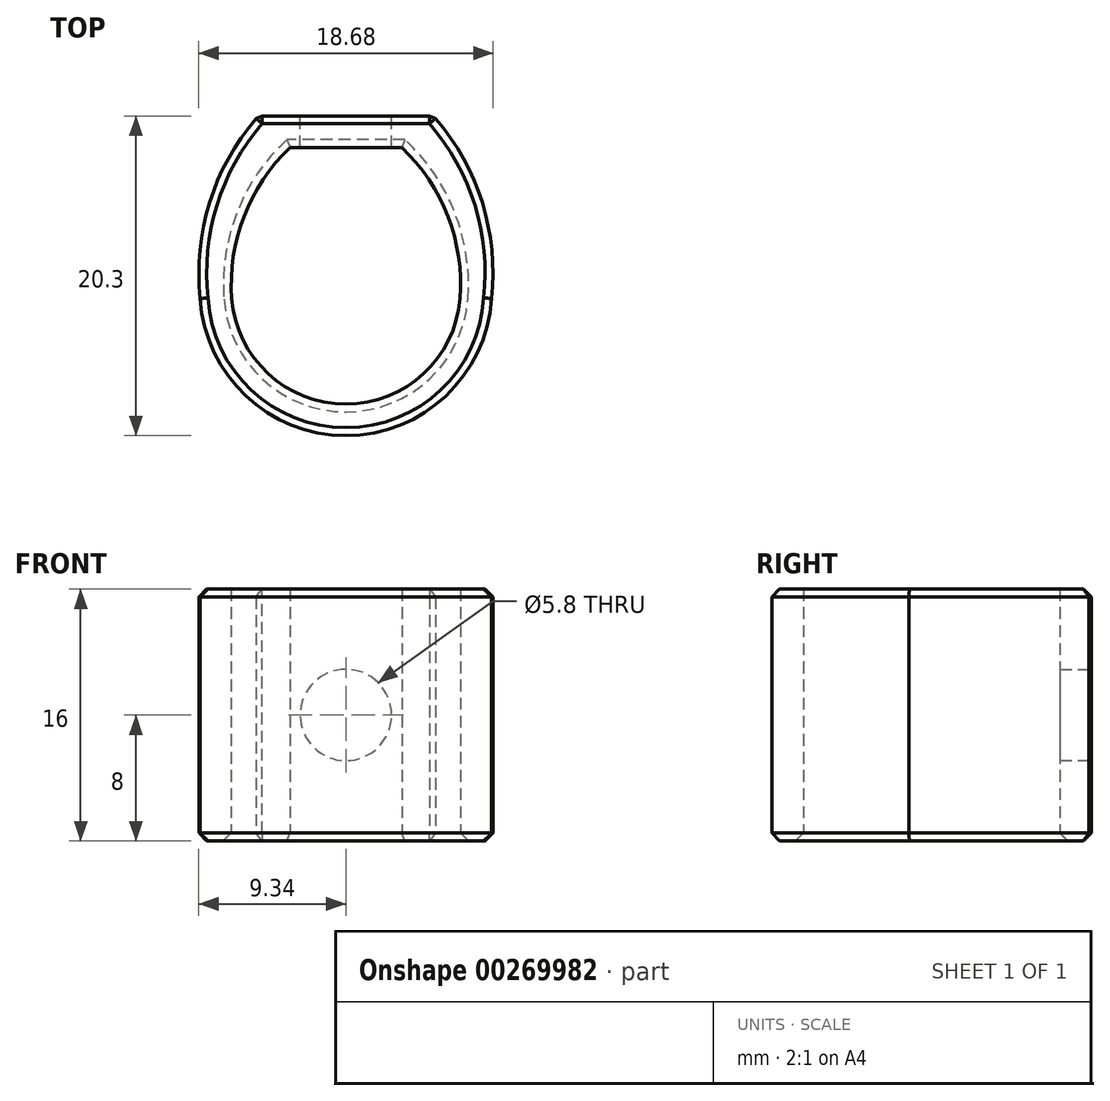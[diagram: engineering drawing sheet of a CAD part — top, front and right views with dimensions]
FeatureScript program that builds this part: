
annotation { "Feature Type Name" : "Feature", "Feature Type Description" : "" }
export const myFeature = defineFeature(function(context is Context, id is Id, definition is map)
    precondition{}
    {
        {
            var Q0;
            Q0=qCreatedBy(makeId("Top.planeOp"),FACE);
            var sketch = newSketch(context, id + "F0", { "sketchPlane" : qUnion([Q0])});
            skPoint(sketch, "E0", {"position": v(-7.25, 0) * mm});
            skPoint(sketch, "E1", {"position": v(7.25, 0) * mm});
            skPoint(sketch, "E2", {"position": v(0, 9.6) * mm});
            skPoint(sketch, "E3", {"position": v(0, -6.7) * mm});
            skCircle(sketch, "E4", {"center": v(0, 0) * mm, "radius": 5 * mm, "construction": true});
            skLineSegment(sketch, "E5", {"start": v(-3.55, 9.6) * mm, "end": v(3.55, 9.6) * mm});
            skArc(sketch, "E6", {"start": v(-7.25, 0) * mm, "mid": v(0, -6.7) * mm, "end": v(7.25, 0) * mm});
            skArc(sketch, "E7", {"start": v(-3.55, 9.6) * mm, "mid": v(-6.48, 5.22) * mm, "end": v(-7.25, 0) * mm});
            skArc(sketch, "E8.MirrorCS", {"start": v(3.55, 9.6) * mm, "mid": v(6.48, 5.22) * mm, "end": v(7.25, 0) * mm});
            skPoint(sketch, "E9", {"position": v(-9.25, 0) * mm});
            skPoint(sketch, "E10", {"position": v(9.25, 0) * mm});
            skPoint(sketch, "E11", {"position": v(0, -8.7) * mm});
            skArc(sketch, "E12", {"start": v(-9.25, 0) * mm, "mid": v(0, -8.7) * mm, "end": v(9.25, 0) * mm});
            skPoint(sketch, "E13", {"position": v(-5.55, 11.6) * mm});
            skPoint(sketch, "E14.MirrorP", {"position": v(5.55, 11.6) * mm});
            skArc(sketch, "E15", {"start": v(-5.55, 11.6) * mm, "mid": v(-8.63, 6.2) * mm, "end": v(-9.25, 0) * mm});
            skArc(sketch, "E16.MirrorCS", {"start": v(5.55, 11.6) * mm, "mid": v(8.63, 6.2) * mm, "end": v(9.25, 0) * mm});
            skLineSegment(sketch, "E17", {"start": v(-5.55, 11.6) * mm, "end": v(5.55, 11.6) * mm});
            skSolve(sketch);
        }
        {
            var Q0;
            Q0=makeQuery(id+"F0.imprint","IMPRINT",FACE,{"disambiguationData":[TD([[makeQuery(id+"F0.imprint","IMPRINT",EDGE,{"derivedFrom":sQuery(id+"F0.wireOp",EDGE,"E5")}),1.0]])]});
            extrude(context, id + "F1", {"entities" : qUnion([Q0]), "depth" : 16 * mm, "offsetDistance" : 25 * mm});
        }
        {
            var Q0;
            Q0=makeQuery(id+"F1.opExtrude","SWEPT_FACE",FACE,{"disambiguationData":[OSD([sQuery(id+"F0.wireOp",EDGE,"E17")])]});
            var sketch = newSketch(context, id + "F2", { "sketchPlane" : qUnion([Q0])});
            skPoint(sketch, "E18", {"position": v(0, 8) * mm});
            skPoint(sketch, "E18.positionSnap0", {"position": v(-5.55, 8) * mm});
            skPoint(sketch, "E18.positionSnap1", {"position": v(0, 16) * mm});
            skCircle(sketch, "E19", {"center": v(0, 8) * mm, "radius": 2.9 * mm});
            skSolve(sketch);
        }
        {
            var Q0;
            Q0=makeQuery(id+"F2.imprint","IMPRINT",FACE,{"disambiguationData":[TD([[makeQuery(id+"F2.imprint","IMPRINT",EDGE,{"derivedFrom":sQuery(id+"F2.wireOp",EDGE,"E19")}),1.0]])]});
            var Q1;
            Q1=makeQuery(id+"F1.opExtrude","SWEPT_FACE",FACE,{"disambiguationData":[OSD([sQuery(id+"F0.wireOp",EDGE,"E5")])]});
            extrude(context, id + "F3", {"entities" : qUnion([Q0]), "operationType" : NewBodyOperationType.REMOVE, "endBound" : BoundingType.UP_TO_SURFACE, "oppositeDirection" : true, "depth" : 25 * mm, "endBoundEntityFace" : qUnion([Q1]), "offsetDistance" : 25 * mm});
        }
        {
            var Q0;
            Q0=makeQuery(id+"F3.boolean.opBoolean","COPY",EDGE,{"derivedFrom":makeQuery(id+"F3.opExtrude","CAP_EDGE",EDGE,{"disambiguationData":[OSD([sQuery(id+"F2.wireOp",EDGE,"E19")])],"isStart":true})});
            var Q1;
            Q1=makeQuery(id+"F1.opExtrude","CAP_EDGE",EDGE,{"disambiguationData":[OSD([sQuery(id+"F0.wireOp",EDGE,"E17")])],"isStart":false});
            var Q2;
            Q2=makeQuery(id+"F1.opExtrude","CAP_EDGE",EDGE,{"disambiguationData":[OSD([sQuery(id+"F0.wireOp",EDGE,"E15")])],"isStart":false});
            var Q3;
            Q3=makeQuery(id+"F1.opExtrude","CAP_EDGE",EDGE,{"disambiguationData":[OSD([sQuery(id+"F0.wireOp",EDGE,"E12")])],"isStart":false});
            var Q4;
            Q4=makeQuery(id+"F1.opExtrude","CAP_EDGE",EDGE,{"disambiguationData":[OSD([sQuery(id+"F0.wireOp",EDGE,"E17")])],"isStart":true});
            var Q5;
            Q5=makeQuery(id+"F1.opExtrude","CAP_EDGE",EDGE,{"disambiguationData":[OSD([sQuery(id+"F0.wireOp",EDGE,"E15")])],"isStart":true});
            var Q6;
            Q6=makeQuery(id+"F1.opExtrude","CAP_EDGE",EDGE,{"disambiguationData":[OSD([sQuery(id+"F0.wireOp",EDGE,"E16.MirrorCS")])],"isStart":true});
            var Q7;
            Q7=makeQuery(id+"F1.opExtrude","CAP_EDGE",EDGE,{"disambiguationData":[OSD([sQuery(id+"F0.wireOp",EDGE,"E12")])],"isStart":true});
            var Q8;
            Q8=makeQuery(id+"F1.opExtrude","CAP_EDGE",EDGE,{"disambiguationData":[OSD([sQuery(id+"F0.wireOp",EDGE,"E8.MirrorCS")])],"isStart":true});
            var Q9;
            Q9=makeQuery(id+"F1.opExtrude","CAP_EDGE",EDGE,{"disambiguationData":[OSD([sQuery(id+"F0.wireOp",EDGE,"E5")])],"isStart":true});
            var Q10;
            Q10=makeQuery(id+"F1.opExtrude","CAP_EDGE",EDGE,{"disambiguationData":[OSD([sQuery(id+"F0.wireOp",EDGE,"E7")])],"isStart":true});
            var Q11;
            Q11=makeQuery(id+"F1.opExtrude","SWEPT_EDGE",EDGE,{"disambiguationData":[OSD([sQuery(id+"F0.wireOp",EDGE,"E15"),sQuery(id+"F0.wireOp",EDGE,"E17")])]});
            var Q12;
            Q12=makeQuery(id+"F1.opExtrude","SWEPT_EDGE",EDGE,{"disambiguationData":[OSD([sQuery(id+"F0.wireOp",EDGE,"E16.MirrorCS"),sQuery(id+"F0.wireOp",EDGE,"E17")])]});
            chamfer(context, id + "F4", {"entities" : qUnion([Q0, Q1, Q2, Q3, Q4, Q5, Q6, Q7, Q8, Q9, Q10, Q11, Q12]), "width" : 0.5 * mm, "tangentPropagation" : true});
        }
    });
